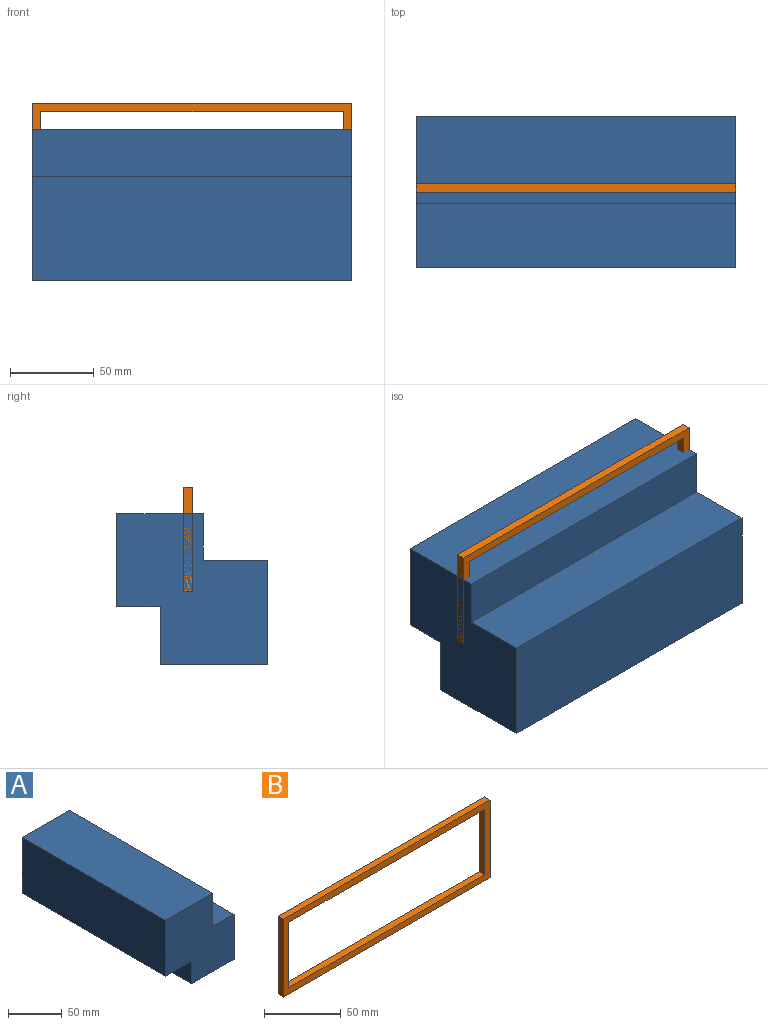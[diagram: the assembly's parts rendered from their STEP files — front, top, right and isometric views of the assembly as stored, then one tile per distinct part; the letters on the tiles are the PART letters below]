
ASSEMBLY  parts=2 mates=1
PART A: 10 faces, bbox 90x190x89.6 mm
  f0: plane 190x27.77mm, normal (0,0,1), area 5276mm2, adj f1,f7,f8,f9
  f1: plane 190x37.97mm, normal (1,0,0), area 7213.9mm2, adj f0,f2,f8,f9
  f2: plane 190x62.26mm, normal (0,0,1), area 11828.5mm2, adj f1,f3,f8,f9
  f3: plane 190x63.77mm, normal (-1,0,0), area 12115.6mm2, adj f2,f4,f8,f9
  f4: plane 190x34.49mm, normal (0,0,-1), area 6552.5mm2, adj f3,f5,f8,f9
  f5: plane 190x25.8mm, normal (-1,0,0), area 4901.8mm2, adj f4,f6,f8,f9
  f6: plane 190x55.54mm, normal (0,0,-1), area 10552mm2, adj f5,f7,f8,f9
  f7: plane 190x51.6mm, normal (1,0,0), area 9803.6mm2, adj f0,f6,f8,f9
  f8: plane 90.02x89.57mm, normal (0,1,0), area 6119mm2, adj f0,f1,f2,f3,f4,f5,f6,f7
  f9: plane 90.02x89.57mm, normal (0,-1,0), area 6119mm2, adj f0,f1,f2,f3,f4,f5,f6,f7
PART B: 10 faces, bbox 190x5x62 mm
  f0: plane 190x5mm, normal (0,0,-1), area 950mm2, adj f1,f7,f8,f9
  f1: plane 62x5mm, normal (1,0,0), area 310mm2, adj f0,f2,f8,f9
  f2: plane 190x5mm, normal (0,0,1), area 950mm2, adj f1,f7,f8,f9
  f3: plane 52x5mm, normal (1,0,0), area 260mm2, adj f4,f6,f8,f9
  f4: plane 180x5mm, normal (0,0,-1), area 900mm2, adj f3,f5,f8,f9
  f5: plane 52x5mm, normal (-1,0,0), area 260mm2, adj f4,f6,f8,f9
  f6: plane 180x5mm, normal (0,0,1), area 900mm2, adj f3,f5,f8,f9
  f7: plane 62x5mm, normal (-1,0,0), area 310mm2, adj f0,f2,f8,f9
  f8: plane 190x62mm, normal (0,-1,0), area 2420mm2, adj f0,f1,f2,f3,f4,f5,f6,f7
  f9: plane 190x62mm, normal (0,1,0), area 2420mm2, adj f0,f1,f2,f3,f4,f5,f6,f7
PLACE A rot(axis=(0.58,-0.58,0.58),120deg) t=(3.31,39.52,4.22)mm
PLACE B t=(8.31,25.35,-9.35)mm
MATE fastened A.f8 <-> B.f7  axis (-1,0,0) through (3.31,20.35,-14.35)mm
